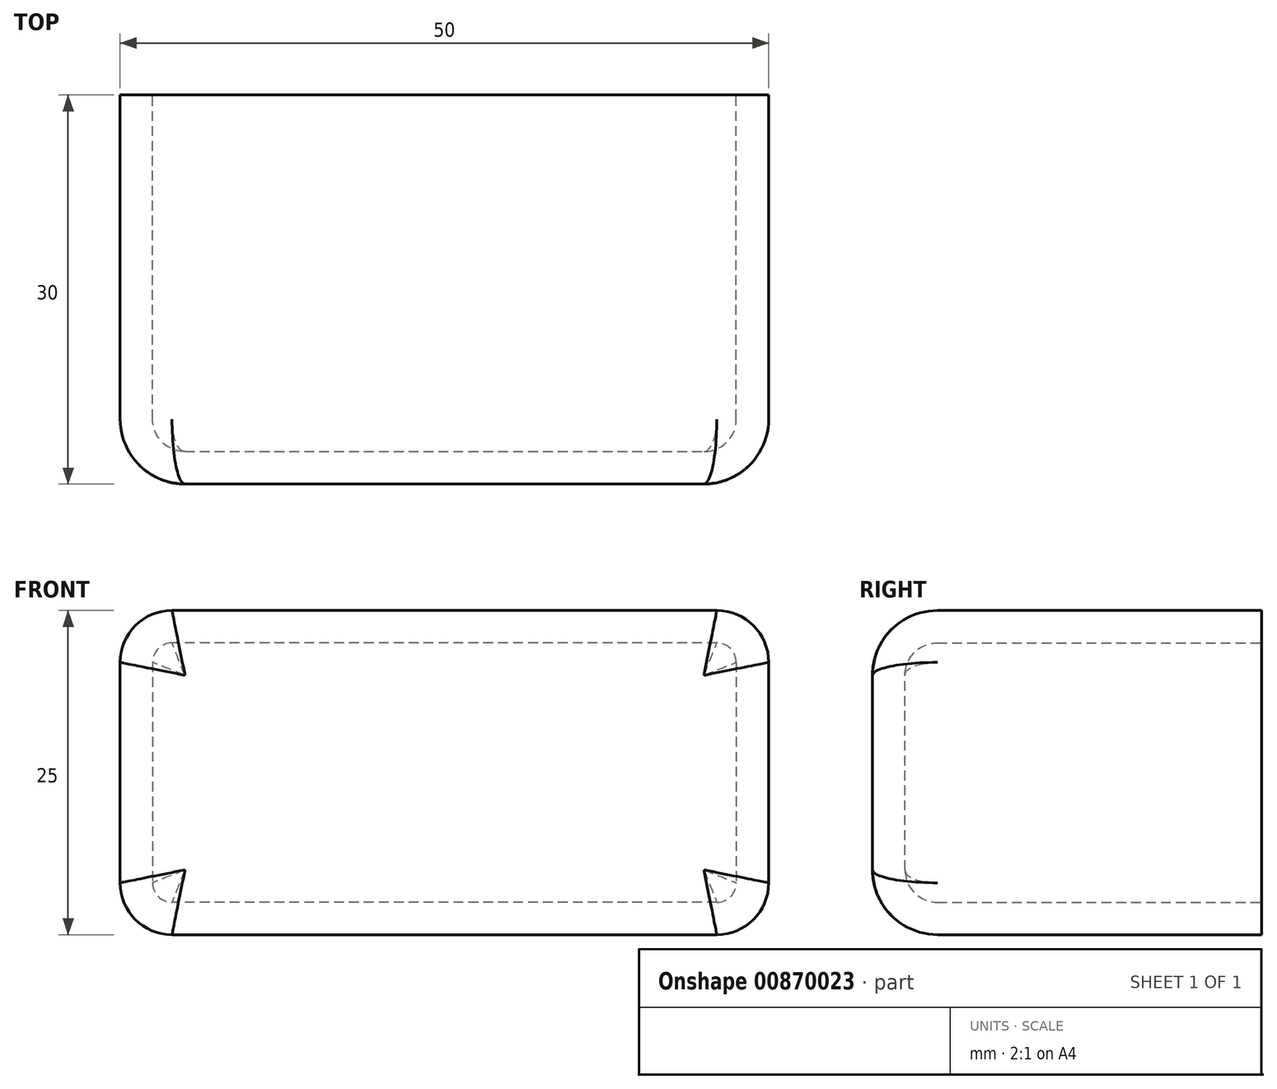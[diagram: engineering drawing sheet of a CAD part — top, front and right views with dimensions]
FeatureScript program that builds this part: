
annotation { "Feature Type Name" : "Feature", "Feature Type Description" : "" }
export const myFeature = defineFeature(function(context is Context, id is Id, definition is map)
    precondition{}
    {
        {
            var Q0;
            Q0=qCreatedBy(makeId("Front.planeOp"),FACE);
            var sketch = newSketch(context, id + "F0", { "sketchPlane" : qUnion([Q0])});
            skLineSegment(sketch, "E0.bottom", {"start": v(21, 12.5) * mm, "end": v(-21, 12.5) * mm});
            skLineSegment(sketch, "E0.top", {"start": v(21, -12.5) * mm, "end": v(-21, -12.5) * mm});
            skLineSegment(sketch, "E0.left", {"start": v(25, 8.5) * mm, "end": v(25, -8.5) * mm});
            skLineSegment(sketch, "E0.right", {"start": v(-25, 8.5) * mm, "end": v(-25, -8.5) * mm});
            skPoint(sketch, "E0.middle", {"position": v(0, 0) * mm});
            skPoint(sketch, "E1.visualSharp", {"position": v(25, 12.5) * mm});
            skArc(sketch, "E1.filletArc", {"start": v(25, 8.5) * mm, "mid": v(23.83, 11.33) * mm, "end": v(21, 12.5) * mm});
            skPoint(sketch, "E2.visualSharp", {"position": v(25, -12.5) * mm});
            skArc(sketch, "E2.filletArc", {"start": v(21, -12.5) * mm, "mid": v(23.83, -11.33) * mm, "end": v(25, -8.5) * mm});
            skPoint(sketch, "E3.visualSharp", {"position": v(-25, -12.5) * mm});
            skArc(sketch, "E3.filletArc", {"start": v(-25, -8.5) * mm, "mid": v(-23.83, -11.33) * mm, "end": v(-21, -12.5) * mm});
            skPoint(sketch, "E4.visualSharp", {"position": v(-25, 12.5) * mm});
            skArc(sketch, "E4.filletArc", {"start": v(-21, 12.5) * mm, "mid": v(-23.83, 11.33) * mm, "end": v(-25, 8.5) * mm});
            skSolve(sketch);
        }
        {
            var Q0;
            Q0 = qSketchRegion(id + "F0", true);
            extrude(context, id + "F1", {"entities" : qUnion([Q0]), "depth" : 30 * mm, "offsetDistance" : 25 * mm});
        }
        {
            var Q0;
            Q0=makeQuery(id+"F1.opExtrude","CAP_FACE",FACE,{"disambiguationData":[OSD([sQuery(id+"F0.wireOp",EDGE,"E0.bottom"),sQuery(id+"F0.wireOp",EDGE,"E0.top"),sQuery(id+"F0.wireOp",EDGE,"E0.left"),sQuery(id+"F0.wireOp",EDGE,"E0.right"),sQuery(id+"F0.wireOp",EDGE,"E1.filletArc"),sQuery(id+"F0.wireOp",EDGE,"E2.filletArc"),sQuery(id+"F0.wireOp",EDGE,"E3.filletArc"),sQuery(id+"F0.wireOp",EDGE,"E4.filletArc")])],"isStart":false});
            fillet(context, id + "F2", {"entities" : qUnion([Q0]), "radius" : 5 * mm, "tangentPropagation" : true, "allowEdgeOverflow" : false});
        }
        {
            var Q0;
            Q0=makeQuery(id+"F1.opExtrude","CAP_FACE",FACE,{"disambiguationData":[OSD([sQuery(id+"F0.wireOp",EDGE,"E0.bottom"),sQuery(id+"F0.wireOp",EDGE,"E0.top"),sQuery(id+"F0.wireOp",EDGE,"E0.left"),sQuery(id+"F0.wireOp",EDGE,"E0.right"),sQuery(id+"F0.wireOp",EDGE,"E1.filletArc"),sQuery(id+"F0.wireOp",EDGE,"E2.filletArc"),sQuery(id+"F0.wireOp",EDGE,"E3.filletArc"),sQuery(id+"F0.wireOp",EDGE,"E4.filletArc")])],"isStart":true});
            shell(context, id + "F3", {"entities" : qUnion([Q0]), "thickness" : 2.5 * mm});
        }
    });
